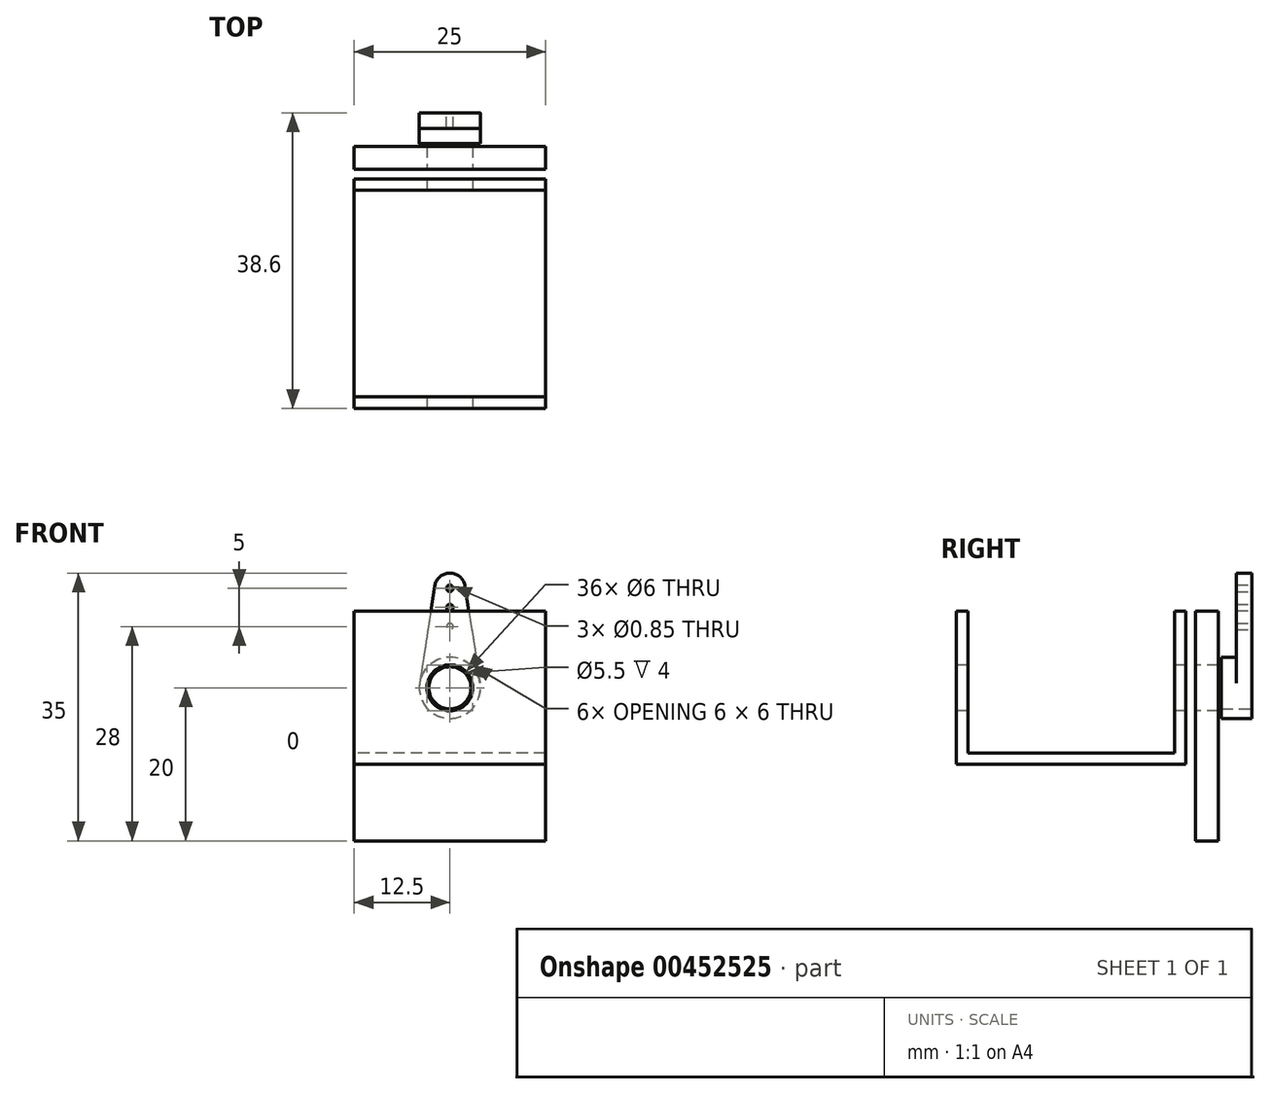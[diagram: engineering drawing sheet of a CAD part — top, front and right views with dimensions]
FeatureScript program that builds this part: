
annotation { "Feature Type Name" : "Feature", "Feature Type Description" : "" }
export const myFeature = defineFeature(function(context is Context, id is Id, definition is map)
    precondition{}
    {
        {
            var Q0;
            Q0=qCreatedBy(makeId("Front.planeOp"),FACE);
            var sketch = newSketch(context, id + "F0", { "sketchPlane" : qUnion([Q0])});
            skCircle(sketch, "E0", {"center": v(0, 0) * mm, "radius": 4 * mm});
            skCircle(sketch, "E1", {"center": v(0, 13) * mm, "radius": 2 * mm});
            skLineSegment(sketch, "E2", {"start": v(-1.98, 13.3) * mm, "end": v(-3.95, 0.62) * mm});
            skLineSegment(sketch, "E3", {"start": v(1.98, 13.3) * mm, "end": v(3.95, 0.62) * mm});
            skLineSegment(sketch, "E4", {"start": v(0, 13) * mm, "end": v(0, 0) * mm, "construction": true});
            skCircle(sketch, "E5", {"center": v(0, 0) * mm, "radius": 2.75 * mm});
            skCircle(sketch, "E6.0.1.0", {"center": v(0, 10.5) * mm, "radius": 0.42 * mm});
            skLineSegment(sketch, "E6.direction2", {"start": v(0, 13) * mm, "end": v(0, 10.5) * mm, "construction": true});
            skCircle(sketch, "E7.0.1.0", {"center": v(0, 8) * mm, "radius": 0.42 * mm});
            skLineSegment(sketch, "E8", {"start": v(0, 10.5) * mm, "end": v(0, 8) * mm, "construction": true});
            skCircle(sketch, "E9", {"center": v(0, 13) * mm, "radius": 0.42 * mm});
            skSolve(sketch);
        }
        {
            var Q0;
            {var subQ0=sQuery(id+"F0.wireOp",EDGE,"E2");Q0=makeQuery(id+"F0.imprint","IMPRINT",FACE,{"disambiguationData":[TD([[makeQuery(id+"F0.imprint","IMPRINT",EDGE,{"derivedFrom":subQ0}),1.0]])]});}
            var Q1;
            Q1=makeQuery(id+"F0.imprint","IMPRINT",FACE,{"disambiguationData":[TD([[makeQuery(id+"F0.imprint","IMPRINT",EDGE,{"derivedFrom":sQuery(id+"F0.wireOp",EDGE,"E9")}),-1.0]])]});
            extrude(context, id + "F1", {"entities" : qUnion([Q0, Q1]), "depth" : 2 * mm});
        }
        {
            var Q0;
            Q0=makeQuery(id+"F0.imprint","IMPRINT",FACE,{"disambiguationData":[TD([[makeQuery(id+"F0.imprint","IMPRINT",EDGE,{"derivedFrom":sQuery(id+"F0.wireOp",EDGE,"E5")}),-1.0]])]});
            extrude(context, id + "F2", {"entities" : qUnion([Q0]), "operationType" : NewBodyOperationType.ADD, "depth" : 4 * mm});
        }
        {
            var Q0;
            Q0=qCreatedBy(makeId("Right.planeOp"),FACE);
            var sketch = newSketch(context, id + "F3", { "sketchPlane" : qUnion([Q0])});
            skLineSegment(sketch, "E10", {"start": v(23.98, 0) * mm, "end": v(-34.81, 0) * mm, "construction": true});
            skLineSegment(sketch, "E11.bottom", {"start": v(-38.6, 10) * mm, "end": v(-8.6, 10) * mm});
            skLineSegment(sketch, "E11.top", {"start": v(-38.6, -10) * mm, "end": v(-8.6, -10) * mm});
            skLineSegment(sketch, "E11.left", {"start": v(-38.6, 10) * mm, "end": v(-38.6, -10) * mm});
            skLineSegment(sketch, "E11.right", {"start": v(-8.6, 10) * mm, "end": v(-8.6, -10) * mm});
            skLineSegment(sketch, "E12.bottom", {"start": v(-7.35, 10) * mm, "end": v(-4.35, 10) * mm});
            skLineSegment(sketch, "E12.top", {"start": v(-7.35, -20) * mm, "end": v(-4.35, -20) * mm});
            skLineSegment(sketch, "E12.left", {"start": v(-7.35, 10) * mm, "end": v(-7.35, -20) * mm});
            skLineSegment(sketch, "E12.right", {"start": v(-4.35, 10) * mm, "end": v(-4.35, -20) * mm});
            skSolve(sketch);
        }
        {
            var Q0;
            Q0=makeQuery(id+"F3.imprint","IMPRINT",FACE,{"disambiguationData":[TD([[makeQuery(id+"F3.imprint","IMPRINT",EDGE,{"derivedFrom":sQuery(id+"F3.wireOp",EDGE,"E11.bottom")}),-1.0]])]});
            extrude(context, id + "F4", {"entities" : qUnion([Q0]), "depth" : 25 * mm, "symmetric" : true});
        }
        {
            var Q0;
            Q0=makeQuery(id+"F4.opExtrude","CAP_FACE",FACE,{"disambiguationData":[OSD([sQuery(id+"F3.wireOp",EDGE,"E11.bottom"),sQuery(id+"F3.wireOp",EDGE,"E11.top"),sQuery(id+"F3.wireOp",EDGE,"E11.left"),sQuery(id+"F3.wireOp",EDGE,"E11.right")])],"isStart":false});
            var Q1;
            Q1=makeQuery(id+"F4.opExtrude","SWEPT_FACE",FACE,{"disambiguationData":[OSD([sQuery(id+"F3.wireOp",EDGE,"E11.bottom")])]});
            var Q2;
            Q2=makeQuery(id+"F4.opExtrude","CAP_FACE",FACE,{"disambiguationData":[OSD([sQuery(id+"F3.wireOp",EDGE,"E11.bottom"),sQuery(id+"F3.wireOp",EDGE,"E11.top"),sQuery(id+"F3.wireOp",EDGE,"E11.left"),sQuery(id+"F3.wireOp",EDGE,"E11.right")])],"isStart":true});
            shell(context, id + "F5", {"entities" : qUnion([Q0, Q1, Q2]), "thickness" : 1.5 * mm});
        }
        {
            var Q0;
            Q0=makeQuery(id+"F3.imprint","IMPRINT",FACE,{"disambiguationData":[TD([[makeQuery(id+"F3.imprint","IMPRINT",EDGE,{"derivedFrom":sQuery(id+"F3.wireOp",EDGE,"E12.bottom")}),-1.0]])]});
            extrude(context, id + "F6", {"entities" : qUnion([Q0]), "depth" : 25 * mm, "symmetric" : true});
        }
        {
            var Q0;
            Q0=makeQuery(id+"F4.opExtrude","SWEPT_FACE",FACE,{"disambiguationData":[OSD([sQuery(id+"F3.wireOp",EDGE,"E11.left")])]});
            var sketch = newSketch(context, id + "F7", { "sketchPlane" : qUnion([Q0])});
            skCircle(sketch, "E13", {"center": v(0, 0) * mm, "radius": 3 * mm});
            skSolve(sketch);
        }
        {
            var Q0;
            Q0=makeQuery(id+"F7.imprint","IMPRINT",FACE,{"disambiguationData":[TD([[makeQuery(id+"F7.imprint","IMPRINT",EDGE,{"derivedFrom":sQuery(id+"F7.wireOp",EDGE,"E13")}),1.0]])]});
            extrude(context, id + "F8", {"entities" : qUnion([Q0]), "endBound" : BoundingType.THROUGH_ALL, "oppositeDirection" : true, "depth" : 25 * mm});
        }
        {
            var Q0;
            Q0=makeQuery(id+"F8.opExtrude","SWEPT_BODY",BODY,{"disambiguationData":[OSD([sQuery(id+"F7.wireOp",EDGE,"E13")])]});
            var Q1;
            Q1=makeQuery(id+"F4.opExtrude","SWEPT_BODY",BODY,{"disambiguationData":[OSD([sQuery(id+"F3.wireOp",EDGE,"E11.bottom"),sQuery(id+"F3.wireOp",EDGE,"E11.top"),sQuery(id+"F3.wireOp",EDGE,"E11.left"),sQuery(id+"F3.wireOp",EDGE,"E11.right")])]});
            var Q2;
            Q2=makeQuery(id+"F6.opExtrude","SWEPT_BODY",BODY,{"disambiguationData":[OSD([sQuery(id+"F3.wireOp",EDGE,"E12.bottom"),sQuery(id+"F3.wireOp",EDGE,"E12.top"),sQuery(id+"F3.wireOp",EDGE,"E12.left"),sQuery(id+"F3.wireOp",EDGE,"E12.right")])]});
            booleanBodies(context, id + "F9", {"operationType" : BooleanOperationType.SUBTRACTION, "tools" : qUnion([Q0]), "targets" : qUnion([Q1, Q2])});
        }
    });
